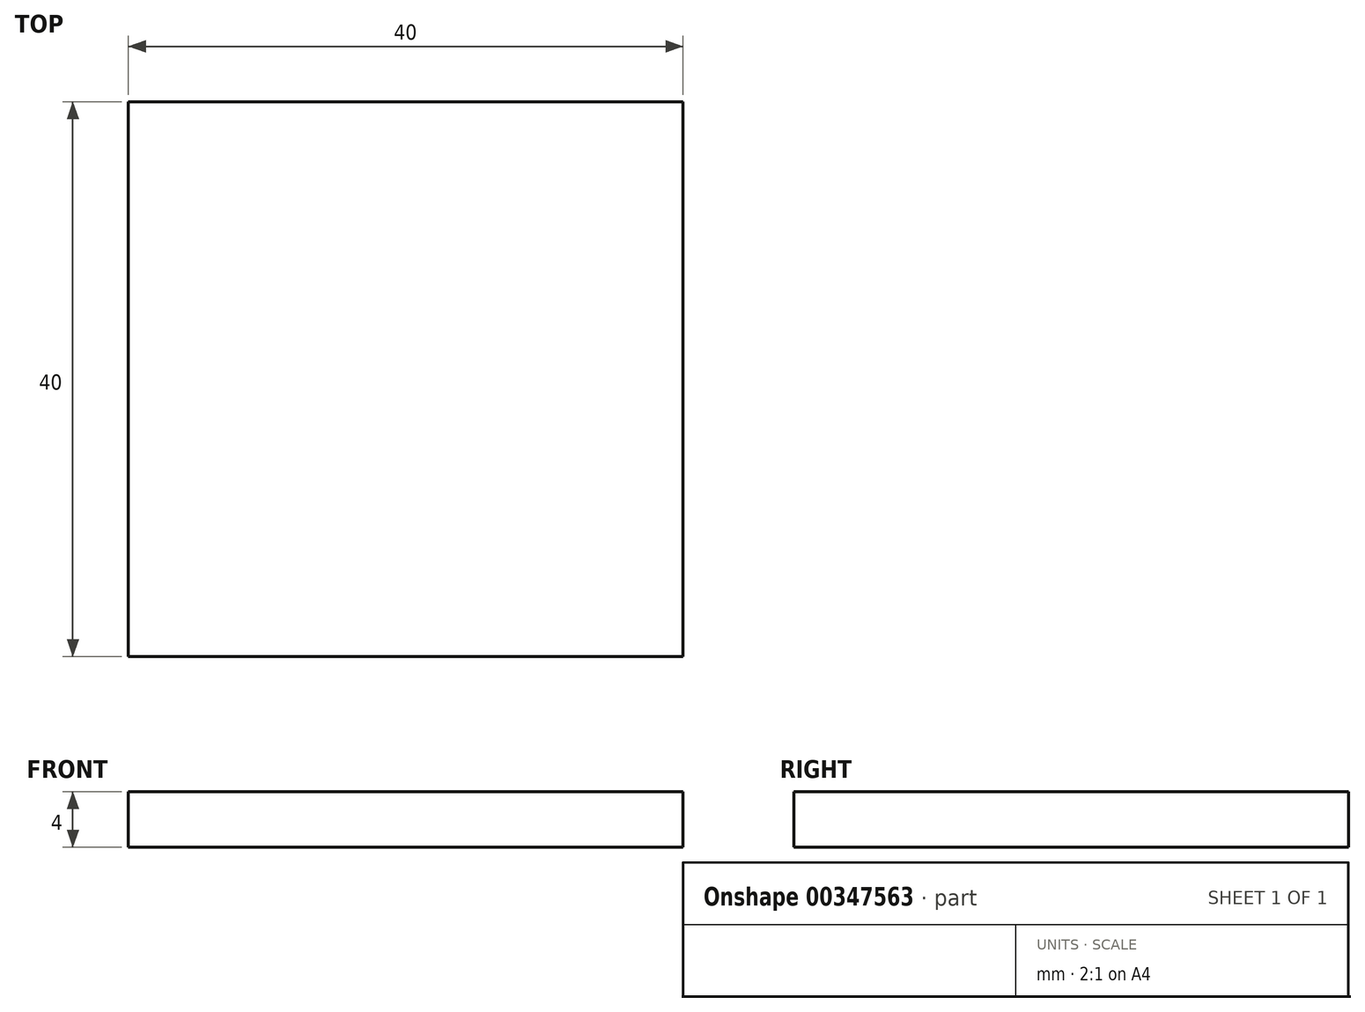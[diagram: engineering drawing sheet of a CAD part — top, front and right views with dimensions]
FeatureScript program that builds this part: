
annotation { "Feature Type Name" : "Feature", "Feature Type Description" : "" }
export const myFeature = defineFeature(function(context is Context, id is Id, definition is map)
    precondition{}
    {
        {
            var Q0;
            Q0=qCreatedBy(makeId("Top.planeOp"),FACE);
            var sketch = newSketch(context, id + "F0", { "sketchPlane" : qUnion([Q0])});
            skLineSegment(sketch, "E0.bottom", {"start": v(20, -20) * mm, "end": v(-20, -20) * mm});
            skLineSegment(sketch, "E0.top", {"start": v(20, 20) * mm, "end": v(-20, 20) * mm});
            skLineSegment(sketch, "E0.left", {"start": v(20, -20) * mm, "end": v(20, 20) * mm});
            skLineSegment(sketch, "E0.right", {"start": v(-20, -20) * mm, "end": v(-20, 20) * mm});
            skPoint(sketch, "E0.middle", {"position": v(0, 0) * mm});
            skSolve(sketch);
        }
        {
            var Q0;
            Q0=makeQuery(id+"F0.imprint","IMPRINT",FACE,{"disambiguationData":[TD([[makeQuery(id+"F0.imprint","IMPRINT",EDGE,{"derivedFrom":sQuery(id+"F0.wireOp",EDGE,"E0.bottom")}),-1.0]])]});
            extrude(context, id + "F1", {"entities" : qUnion([Q0]), "depth" : 4 * mm});
        }
    });
